# Revit family: TAG1
name_source: partatom
category: Furniture
units: mm (PartAtom-declared; Revit-internal decimal feet)

## family parameters
Always vertical = Yes
Cut with Voids When Loaded = No
OmniClass Number = 23.40.20.00
OmniClass Title = General Furniture and Specialties
Render Appearance Source = Family Geometry
Room Calculation Point = No
Shared = No
Work Plane-Based = No

## types (1)
- CW001
    Default Elevation = 0 mm  [stored 0 ft]
    Description = 2 x CaseWorks Countertop Laminate 24Dx90W, 2 x CaseWorks Toe Kick 04Hx30W (Cut to size on-site), 2 x CaseWorks Toe Kick 04Hx90W (Cut to size on-site), 1 x CaseWorks Base Cabinet Double Doors 35Hx36Wx24D, 2 x CaseWorks Base Cabinet Three Drawers 35Hx36Wx24D, 2 x CaseWorks Base Cabinet Open 35Hx36Wx24D, 2 x CaseWorks Storage Cabinet Open 84Hx15Wx24D, 1 x CaseWorks Storage Cabinet Single Door Left 84Hx15Wx24D, 1 x CaseWorks Storage Cabinet Single Door Right 84Hx15Wx24D, 2 x 86 Degree Hinge Restriction Clip
    Exported From CET Designer = Yes
    Manufacturer = AIS
    Model = M-ACL2490
    Show CW001 = Yes
    VisibilityIndex = 0

note: [stored X ft] marks values corroborated as IEEE doubles in the binary element streams (Revit-internal decimal feet)

## geometry (parser evidence)
native form markers: Sweep x3
no freeform markers — native parametric forms only
